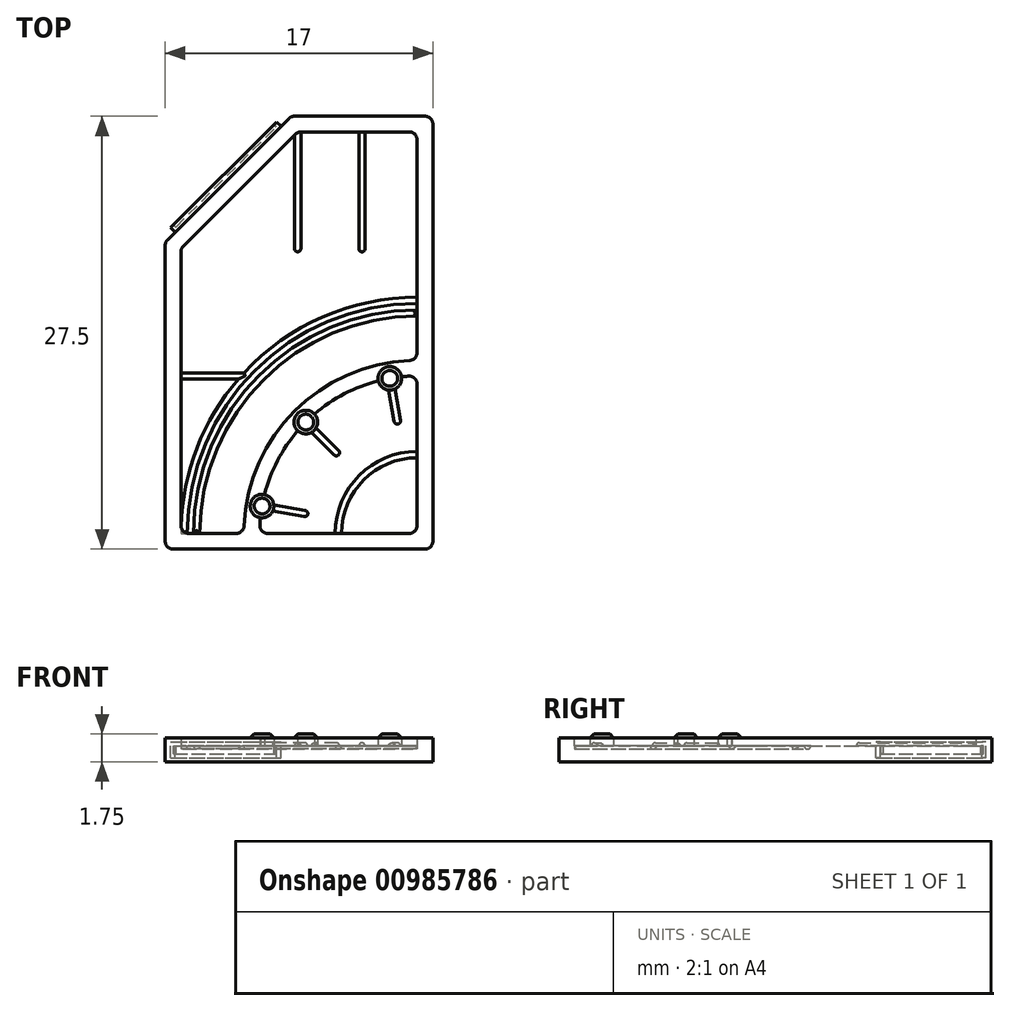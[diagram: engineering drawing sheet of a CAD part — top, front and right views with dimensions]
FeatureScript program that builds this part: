
annotation { "Feature Type Name" : "Feature", "Feature Type Description" : "" }
export const myFeature = defineFeature(function(context is Context, id is Id, definition is map)
    precondition{}
    {
        {
            var Q0;
            Q0=qCreatedBy(makeId("Top.planeOp"),FACE);
            var sketch = newSketch(context, id + "F0", { "sketchPlane" : qUnion([Q0])});
            skLineSegment(sketch, "E0.bottom", {"start": v(-8.5, -13.75) * mm, "end": v(8.5, -13.75) * mm});
            skLineSegment(sketch, "E0.top", {"start": v(-0.5, 13.75) * mm, "end": v(8.5, 13.75) * mm});
            skLineSegment(sketch, "E0.left", {"start": v(-8.5, -13.75) * mm, "end": v(-8.5, 5.75) * mm});
            skLineSegment(sketch, "E0.right", {"start": v(8.5, -13.75) * mm, "end": v(8.5, 13.75) * mm});
            skPoint(sketch, "E0.middle", {"position": v(0, 0) * mm});
            skLineSegment(sketch, "E1", {"start": v(-0.5, 13.75) * mm, "end": v(-8.5, 5.75) * mm});
            skPoint(sketch, "E2.orphan", {"position": v(-8.5, 13.75) * mm});
            skLineSegment(sketch, "E3", {"start": v(-0.5, 13.75) * mm, "end": v(-8.5, 13.75) * mm, "construction": true});
            skLineSegment(sketch, "E4.0", {"start": v(-7.5, -12.75) * mm, "end": v(-7.5, 5.34) * mm});
            skLineSegment(sketch, "E4.1", {"start": v(-0.09, 12.75) * mm, "end": v(-7.5, 5.34) * mm});
            skLineSegment(sketch, "E4.2", {"start": v(-7.5, -12.75) * mm, "end": v(-3.5, -12.75) * mm});
            skLineSegment(sketch, "E4.3", {"start": v(7.5, -12.75) * mm, "end": v(7.5, -2.75) * mm});
            skLineSegment(sketch, "E4.4", {"start": v(-0.09, 12.75) * mm, "end": v(7.5, 12.75) * mm});
            skArc(sketch, "E5", {"start": v(7.5, -2.75) * mm, "mid": v(7, -2.76) * mm, "end": v(6.5, -2.8) * mm});
            skArc(sketch, "E6.0", {"start": v(7.5, -1.75) * mm, "mid": v(-0.28, -4.97) * mm, "end": v(-3.5, -12.75) * mm});
            skLineSegment(sketch, "E7.trimOffspring", {"start": v(-2.5, -12.75) * mm, "end": v(7.5, -12.75) * mm});
            skLineSegment(sketch, "E8.trimOffspring", {"start": v(7.5, -1.75) * mm, "end": v(7.5, 12.75) * mm});
            skLineSegment(sketch, "E9", {"start": v(7.5, -12.75) * mm, "end": v(-2.35, -11.01) * mm, "construction": true});
            skLineSegment(sketch, "E10", {"start": v(7.5, -12.75) * mm, "end": v(0.43, -5.68) * mm, "construction": true});
            skLineSegment(sketch, "E11", {"start": v(7.5, -12.75) * mm, "end": v(5.76, -2.9) * mm, "construction": true});
            skCircle(sketch, "E12", {"center": v(5.76, -2.9) * mm, "radius": 0.75 * mm});
            skCircle(sketch, "E13", {"center": v(0.43, -5.68) * mm, "radius": 0.75 * mm});
            skCircle(sketch, "E14", {"center": v(-2.35, -11.01) * mm, "radius": 0.75 * mm});
            skArc(sketch, "E15.trimOffspring", {"start": v(-2.45, -11.76) * mm, "mid": v(-2.49, -12.25) * mm, "end": v(-2.5, -12.75) * mm});
            skArc(sketch, "E16.trimOffspring", {"start": v(-0.08, -6.23) * mm, "mid": v(-1.37, -8.13) * mm, "end": v(-2.2, -10.28) * mm});
            skArc(sketch, "E17.trimOffspring", {"start": v(5.03, -3.06) * mm, "mid": v(2.88, -3.88) * mm, "end": v(0.98, -5.17) * mm});
            skLineSegment(sketch, "E18", {"start": v(4, 12.75) * mm, "end": v(4, 5.34) * mm, "construction": true});
            skPoint(sketch, "E18.startSnap0", {"position": v(4, 13.75) * mm});
            skLineSegment(sketch, "E19", {"start": v(-0.09, 12.75) * mm, "end": v(-0.09, 5.34) * mm, "construction": true});
            skArc(sketch, "E20.0", {"start": v(7.5, 1.25) * mm, "mid": v(-2.4, -2.85) * mm, "end": v(-6.5, -12.75) * mm, "construction": true});
            skArc(sketch, "E21.0", {"start": v(7.5, 2.05) * mm, "mid": v(-2.97, -2.28) * mm, "end": v(-7.3, -12.75) * mm, "construction": true});
            skLineSegment(sketch, "E22", {"start": v(-7.5, -2.75) * mm, "end": v(-3.41, -2.75) * mm, "construction": true});
            skLineSegment(sketch, "E23", {"start": v(-7.5, -2.75) * mm, "end": v(-7.5, -12.75) * mm, "construction": true});
            skLineSegment(sketch, "E24", {"start": v(5.9, -3.64) * mm, "end": v(6.24, -5.61) * mm});
            skLineSegment(sketch, "E25", {"start": v(0.96, -6.2) * mm, "end": v(2.37, -7.62) * mm});
            skLineSegment(sketch, "E26", {"start": v(-1.6, -11.14) * mm, "end": v(0.36, -11.5) * mm});
            skArc(sketch, "E27", {"start": v(7.5, -7.75) * mm, "mid": v(3.96, -9.21) * mm, "end": v(2.5, -12.75) * mm, "construction": true});
            skLineSegment(sketch, "E28.0", {"start": v(-0.29, 12.75) * mm, "end": v(-0.29, 5.34) * mm});
            skLineSegment(sketch, "E29.0", {"start": v(0.11, 12.75) * mm, "end": v(0.11, 5.34) * mm});
            skLineSegment(sketch, "E30.0", {"start": v(3.8, 12.75) * mm, "end": v(3.8, 5.34) * mm});
            skLineSegment(sketch, "E31.0", {"start": v(4.2, 12.75) * mm, "end": v(4.2, 5.34) * mm});
            skArc(sketch, "E32", {"start": v(0.11, 5.34) * mm, "mid": v(-0.09, 5.14) * mm, "end": v(-0.29, 5.34) * mm});
            skArc(sketch, "E33", {"start": v(4.2, 5.34) * mm, "mid": v(4, 5.14) * mm, "end": v(3.8, 5.34) * mm});
            skArc(sketch, "E34.0", {"start": v(7.5, 1.45) * mm, "mid": v(-2.54, -2.7) * mm, "end": v(-6.7, -12.75) * mm});
            skArc(sketch, "E35.0", {"start": v(7.5, 1.05) * mm, "mid": v(-2.26, -3) * mm, "end": v(-6.3, -12.75) * mm});
            skArc(sketch, "E36.0", {"start": v(7.5, 2.25) * mm, "mid": v(1.5, 1) * mm, "end": v(-3.5, -2.55) * mm});
            skArc(sketch, "E37.0", {"start": v(7.5, 1.85) * mm, "mid": v(-2.82, -2.43) * mm, "end": v(-7.1, -12.75) * mm});
            skLineSegment(sketch, "E38.0", {"start": v(-7.5, -2.95) * mm, "end": v(-3.86, -2.95) * mm});
            skLineSegment(sketch, "E39.0", {"start": v(-7.5, -2.55) * mm, "end": v(-3.5, -2.55) * mm});
            skArc(sketch, "E40.trimOffspring", {"start": v(-3.86, -2.95) * mm, "mid": v(-6.56, -7.52) * mm, "end": v(-7.5, -12.75) * mm});
            skLineSegment(sketch, "E41.0", {"start": v(5.7, -3.65) * mm, "end": v(6.04, -5.64) * mm});
            skLineSegment(sketch, "E42.0", {"start": v(6.09, -3.58) * mm, "end": v(6.44, -5.58) * mm});
            skLineSegment(sketch, "E43.0", {"start": v(0.8, -6.33) * mm, "end": v(2.23, -7.76) * mm});
            skLineSegment(sketch, "E44.0", {"start": v(1.08, -6.05) * mm, "end": v(2.51, -7.48) * mm});
            skLineSegment(sketch, "E45.0", {"start": v(-1.67, -11.34) * mm, "end": v(0.33, -11.69) * mm});
            skLineSegment(sketch, "E46.0", {"start": v(-1.6, -10.94) * mm, "end": v(0.4, -11.3) * mm});
            skArc(sketch, "E47", {"start": v(0.4, -11.3) * mm, "mid": v(0.56, -11.53) * mm, "end": v(0.33, -11.69) * mm});
            skArc(sketch, "E48", {"start": v(2.51, -7.48) * mm, "mid": v(2.51, -7.76) * mm, "end": v(2.23, -7.76) * mm});
            skArc(sketch, "E49", {"start": v(6.44, -5.58) * mm, "mid": v(6.28, -5.8) * mm, "end": v(6.04, -5.64) * mm});
            skArc(sketch, "E50.0", {"start": v(7.5, -7.55) * mm, "mid": v(3.82, -9.07) * mm, "end": v(2.3, -12.75) * mm});
            skArc(sketch, "E51.0", {"start": v(7.5, -7.95) * mm, "mid": v(4.1, -9.36) * mm, "end": v(2.7, -12.75) * mm});
            skSolve(sketch);
        }
        {
            var Q0;
            Q0=makeQuery(id+"F0.imprint","IMPRINT",FACE,{"disambiguationData":[TD([[makeQuery(id+"F0.imprint","IMPRINT",EDGE,{"derivedFrom":sQuery(id+"F0.wireOp",EDGE,"E4.0")}),-1.0]])]});
            var Q1;
            Q1=makeQuery(id+"F0.imprint","IMPRINT",FACE,{"disambiguationData":[TD([[makeQuery(id+"F0.imprint","IMPRINT",EDGE,{"derivedFrom":sQuery(id+"F0.wireOp",EDGE,"E4.3")}),1.0]])]});
            var Q2;
            Q2=makeQuery(id+"F0.imprint","IMPRINT",FACE,{"disambiguationData":[TD([[makeQuery(id+"F0.imprint","IMPRINT",EDGE,{"derivedFrom":sQuery(id+"F0.wireOp",EDGE,"E0.bottom")}),1.0]])]});
            var Q3;
            {var subQ0=sQuery(id+"F0.wireOp",EDGE,"E13");var subQ1=makeQuery(id+"F0.imprint","INTERSECT",VERTEX,{"derivedFrom":[subQ0,sQuery(id+"F0.wireOp",EDGE,"E16.trimOffspring")]});Q3=makeQuery(id+"F0.imprint","IMPRINT",FACE,{"disambiguationData":[TD([[makeQuery(id+"F0.imprint","IMPRINT",EDGE,{"disambiguationData":[TD([[subQ1,1.0]])],"derivedFrom":subQ0}),1.0]])]});}
            var Q4;
            {var subQ0=sQuery(id+"F0.wireOp",EDGE,"E12");var subQ1=makeQuery(id+"F0.imprint","INTERSECT",VERTEX,{"derivedFrom":[sQuery(id+"F0.wireOp",EDGE,"E5"),subQ0]});Q4=makeQuery(id+"F0.imprint","IMPRINT",FACE,{"disambiguationData":[TD([[makeQuery(id+"F0.imprint","IMPRINT",EDGE,{"disambiguationData":[TD([[subQ1,-1.0]])],"derivedFrom":subQ0}),1.0]])]});}
            var Q5;
            {var subQ0=sQuery(id+"F0.wireOp",EDGE,"E14");var subQ1=makeQuery(id+"F0.imprint","INTERSECT",VERTEX,{"derivedFrom":[subQ0,sQuery(id+"F0.wireOp",EDGE,"E15.trimOffspring")]});Q5=makeQuery(id+"F0.imprint","IMPRINT",FACE,{"disambiguationData":[TD([[makeQuery(id+"F0.imprint","IMPRINT",EDGE,{"disambiguationData":[TD([[subQ1,1.0]])],"derivedFrom":subQ0}),1.0]])]});}
            var Q6;
            {var subQ5=sQuery(id+"F0.wireOp",EDGE,"E22");Q6=makeQuery(id+"F0.imprint","IMPRINT",FACE,{"disambiguationData":[TD([[makeQuery(id+"F0.imprint","IMPRINT",EDGE,{"derivedFrom":subQ5}),1.0]])]});}
            var Q7;
            {var subQ6=sQuery(id+"F0.wireOp",EDGE,"E29.0");Q7=makeQuery(id+"F0.imprint","IMPRINT",FACE,{"disambiguationData":[TD([[makeQuery(id+"F0.imprint","IMPRINT",EDGE,{"derivedFrom":subQ6}),-1.0]])]});}
            var Q8;
            {var subQ0=sQuery(id+"F0.wireOp",EDGE,"E30.0");Q8=makeQuery(id+"F0.imprint","IMPRINT",FACE,{"disambiguationData":[TD([[makeQuery(id+"F0.imprint","IMPRINT",EDGE,{"derivedFrom":subQ0}),1.0]])]});}
            var Q9;
            {var subQ0=sQuery(id+"F0.wireOp",EDGE,"E20.0");Q9=makeQuery(id+"F0.imprint","IMPRINT",FACE,{"disambiguationData":[TD([[makeQuery(id+"F0.imprint","IMPRINT",EDGE,{"derivedFrom":subQ0}),-1.0]])]});}
            var Q10;
            {var subQ0=sQuery(id+"F0.wireOp",EDGE,"E6.0");Q10=makeQuery(id+"F0.imprint","IMPRINT",FACE,{"disambiguationData":[TD([[makeQuery(id+"F0.imprint","IMPRINT",EDGE,{"derivedFrom":subQ0}),-1.0]])]});}
            var Q11;
            {var subQ8=sQuery(id+"F0.wireOp",EDGE,"E5");Q11=makeQuery(id+"F0.imprint","IMPRINT",FACE,{"disambiguationData":[TD([[makeQuery(id+"F0.imprint","IMPRINT",EDGE,{"derivedFrom":subQ8}),1.0]])]});}
            var Q12;
            {var subQ0=sQuery(id+"F0.wireOp",EDGE,"E34.0");Q12=makeQuery(id+"F0.imprint","IMPRINT",FACE,{"disambiguationData":[TD([[makeQuery(id+"F0.imprint","IMPRINT",EDGE,{"derivedFrom":subQ0}),1.0]])]});}
            var Q13;
            {var subQ0=sQuery(id+"F0.wireOp",EDGE,"E34.0");Q13=makeQuery(id+"F0.imprint","IMPRINT",FACE,{"disambiguationData":[TD([[makeQuery(id+"F0.imprint","IMPRINT",EDGE,{"derivedFrom":subQ0}),-1.0]])]});}
            var Q14;
            {var subQ0=sQuery(id+"F0.wireOp",EDGE,"E36.0");Q14=makeQuery(id+"F0.imprint","IMPRINT",FACE,{"disambiguationData":[TD([[makeQuery(id+"F0.imprint","IMPRINT",EDGE,{"derivedFrom":subQ0}),1.0]])]});}
            var Q15;
            {var subQ0=sQuery(id+"F0.wireOp",EDGE,"E29.0");Q15=makeQuery(id+"F0.imprint","IMPRINT",FACE,{"disambiguationData":[TD([[makeQuery(id+"F0.imprint","IMPRINT",EDGE,{"derivedFrom":subQ0}),1.0]])]});}
            var Q16;
            {var subQ1=sQuery(id+"F0.wireOp",EDGE,"E43.0");Q16=makeQuery(id+"F0.imprint","IMPRINT",FACE,{"disambiguationData":[TD([[makeQuery(id+"F0.imprint","IMPRINT",EDGE,{"derivedFrom":subQ1}),1.0]])]});}
            var Q17;
            {var subQ0=sQuery(id+"F0.wireOp",EDGE,"E41.0");Q17=makeQuery(id+"F0.imprint","IMPRINT",FACE,{"disambiguationData":[TD([[makeQuery(id+"F0.imprint","IMPRINT",EDGE,{"derivedFrom":subQ0}),1.0]])]});}
            var Q18;
            {var subQ0=sQuery(id+"F0.wireOp",EDGE,"E50.0");Q18=makeQuery(id+"F0.imprint","IMPRINT",FACE,{"disambiguationData":[TD([[makeQuery(id+"F0.imprint","IMPRINT",EDGE,{"derivedFrom":subQ0}),1.0]])]});}
            var Q19;
            {var subQ3=sQuery(id+"F0.wireOp",EDGE,"E45.0");Q19=makeQuery(id+"F0.imprint","IMPRINT",FACE,{"disambiguationData":[TD([[makeQuery(id+"F0.imprint","IMPRINT",EDGE,{"derivedFrom":subQ3}),1.0]])]});}
            extrude(context, id + "F1", {"entities" : qUnion([Q0, Q1, Q2, Q3, Q4, Q5, Q6, Q7, Q8, Q9, Q10, Q11, Q12, Q13, Q14, Q15, Q16, Q17, Q18, Q19]), "oppositeDirection" : true, "depth" : 1 * mm, "offsetDistance" : 25 * mm});
        }
        {
            var Q0;
            Q0=makeQuery(id+"F0.imprint","IMPRINT",FACE,{"disambiguationData":[TD([[makeQuery(id+"F0.imprint","IMPRINT",EDGE,{"derivedFrom":sQuery(id+"F0.wireOp",EDGE,"E0.bottom")}),1.0]])]});
            extrude(context, id + "F2", {"entities" : qUnion([Q0]), "operationType" : NewBodyOperationType.ADD, "depth" : .5 * mm, "offsetDistance" : 25 * mm});
        }
        {
            var Q0;
            {var subQ0=sQuery(id+"F0.wireOp",EDGE,"E14");var subQ1=makeQuery(id+"F0.imprint","INTERSECT",VERTEX,{"derivedFrom":[subQ0,sQuery(id+"F0.wireOp",EDGE,"E15.trimOffspring")]});Q0=makeQuery(id+"F0.imprint","IMPRINT",FACE,{"disambiguationData":[TD([[makeQuery(id+"F0.imprint","IMPRINT",EDGE,{"disambiguationData":[TD([[subQ1,1.0]])],"derivedFrom":subQ0}),1.0]])]});}
            var Q1;
            {var subQ0=sQuery(id+"F0.wireOp",EDGE,"E13");var subQ1=makeQuery(id+"F0.imprint","INTERSECT",VERTEX,{"derivedFrom":[subQ0,sQuery(id+"F0.wireOp",EDGE,"E16.trimOffspring")]});Q1=makeQuery(id+"F0.imprint","IMPRINT",FACE,{"disambiguationData":[TD([[makeQuery(id+"F0.imprint","IMPRINT",EDGE,{"disambiguationData":[TD([[subQ1,1.0]])],"derivedFrom":subQ0}),1.0]])]});}
            var Q2;
            {var subQ0=sQuery(id+"F0.wireOp",EDGE,"E12");var subQ1=makeQuery(id+"F0.imprint","INTERSECT",VERTEX,{"derivedFrom":[sQuery(id+"F0.wireOp",EDGE,"E5"),subQ0]});Q2=makeQuery(id+"F0.imprint","IMPRINT",FACE,{"disambiguationData":[TD([[makeQuery(id+"F0.imprint","IMPRINT",EDGE,{"disambiguationData":[TD([[subQ1,-1.0]])],"derivedFrom":subQ0}),1.0]])]});}
            extrude(context, id + "F3", {"entities" : qUnion([Q0, Q1, Q2]), "operationType" : NewBodyOperationType.ADD, "depth" : .75 * mm, "offsetDistance" : 25 * mm});
        }
        {
            var Q0;
            Q0=makeQuery(id+"F3.opExtrude","CAP_EDGE",EDGE,{"disambiguationData":[OSD([sQuery(id+"F0.wireOp",EDGE,"E12")])],"isStart":false});
            var Q1;
            Q1=makeQuery(id+"F3.opExtrude","CAP_FACE",FACE,{"disambiguationData":[OSD([sQuery(id+"F0.wireOp",EDGE,"E13")])],"isStart":false});
            var Q2;
            Q2=makeQuery(id+"F3.opExtrude","CAP_FACE",FACE,{"disambiguationData":[OSD([sQuery(id+"F0.wireOp",EDGE,"E14")])],"isStart":false});
            chamfer(context, id + "F4", {"entities" : qUnion([Q0, Q1, Q2]), "width" : .25 * mm, "tangentPropagation" : true});
        }
        {
            var Q0;
            {var subQ0=sQuery(id+"F0.wireOp",EDGE,"E1");var subQ1=sQuery(id+"F0.wireOp",EDGE,"E0.left");Q0=makeQuery(id+"F2.boolean.opBoolean","MERGE",EDGE,{"derivedFrom":[makeQuery(id+"F1.opExtrude","SWEPT_EDGE",EDGE,{"disambiguationData":[OSD([subQ1,subQ0])]}),makeQuery(id+"F2.opExtrude","SWEPT_EDGE",EDGE,{"disambiguationData":[OSD([subQ1,subQ0])]})]});}
            var Q1;
            {var subQ0=sQuery(id+"F0.wireOp",EDGE,"E0.left");var subQ1=sQuery(id+"F0.wireOp",EDGE,"E0.bottom");Q1=makeQuery(id+"F2.boolean.opBoolean","MERGE",EDGE,{"derivedFrom":[makeQuery(id+"F1.opExtrude","SWEPT_EDGE",EDGE,{"disambiguationData":[OSD([subQ1,subQ0])]}),makeQuery(id+"F2.opExtrude","SWEPT_EDGE",EDGE,{"disambiguationData":[OSD([subQ1,subQ0])]})]});}
            var Q2;
            {var subQ0=sQuery(id+"F0.wireOp",EDGE,"E0.right");var subQ1=sQuery(id+"F0.wireOp",EDGE,"E0.bottom");Q2=makeQuery(id+"F2.boolean.opBoolean","MERGE",EDGE,{"derivedFrom":[makeQuery(id+"F1.opExtrude","SWEPT_EDGE",EDGE,{"disambiguationData":[OSD([subQ1,subQ0])]}),makeQuery(id+"F2.opExtrude","SWEPT_EDGE",EDGE,{"disambiguationData":[OSD([subQ1,subQ0])]})]});}
            var Q3;
            {var subQ0=sQuery(id+"F0.wireOp",EDGE,"E0.right");var subQ1=sQuery(id+"F0.wireOp",EDGE,"E0.top");Q3=makeQuery(id+"F2.boolean.opBoolean","MERGE",EDGE,{"derivedFrom":[makeQuery(id+"F1.opExtrude","SWEPT_EDGE",EDGE,{"disambiguationData":[OSD([subQ1,subQ0])]}),makeQuery(id+"F2.opExtrude","SWEPT_EDGE",EDGE,{"disambiguationData":[OSD([subQ1,subQ0])]})]});}
            var Q4;
            {var subQ0=sQuery(id+"F0.wireOp",EDGE,"E1");var subQ1=sQuery(id+"F0.wireOp",EDGE,"E0.top");Q4=makeQuery(id+"F2.boolean.opBoolean","MERGE",EDGE,{"derivedFrom":[makeQuery(id+"F1.opExtrude","SWEPT_EDGE",EDGE,{"disambiguationData":[OSD([subQ1,subQ0])]}),makeQuery(id+"F2.opExtrude","SWEPT_EDGE",EDGE,{"disambiguationData":[OSD([subQ1,subQ0])]})]});}
            var Q5;
            Q5=makeQuery(id+"F2.opExtrude","SWEPT_EDGE",EDGE,{"disambiguationData":[OSD([sQuery(id+"F0.wireOp",EDGE,"E4.4"),sQuery(id+"F0.wireOp",EDGE,"E8.trimOffspring")])]});
            var Q6;
            Q6=makeQuery(id+"F2.opExtrude","SWEPT_EDGE",EDGE,{"disambiguationData":[OSD([sQuery(id+"F0.wireOp",EDGE,"E4.1"),sQuery(id+"F0.wireOp",EDGE,"E4.4")])]});
            var Q7;
            Q7=makeQuery(id+"F2.opExtrude","SWEPT_EDGE",EDGE,{"disambiguationData":[OSD([sQuery(id+"F0.wireOp",EDGE,"E4.0"),sQuery(id+"F0.wireOp",EDGE,"E4.1")])]});
            var Q8;
            Q8=makeQuery(id+"F2.opExtrude","SWEPT_EDGE",EDGE,{"disambiguationData":[OSD([sQuery(id+"F0.wireOp",EDGE,"E4.0"),sQuery(id+"F0.wireOp",EDGE,"E4.2")])]});
            var Q9;
            Q9=makeQuery(id+"F2.opExtrude","SWEPT_EDGE",EDGE,{"disambiguationData":[OSD([sQuery(id+"F0.wireOp",EDGE,"E4.2"),sQuery(id+"F0.wireOp",EDGE,"E6.0")])]});
            var Q10;
            Q10=makeQuery(id+"F2.opExtrude","SWEPT_EDGE",EDGE,{"disambiguationData":[OSD([sQuery(id+"F0.wireOp",EDGE,"E6.0"),sQuery(id+"F0.wireOp",EDGE,"E8.trimOffspring")])]});
            var Q11;
            Q11=makeQuery(id+"F2.opExtrude","SWEPT_EDGE",EDGE,{"disambiguationData":[OSD([sQuery(id+"F0.wireOp",EDGE,"E7.trimOffspring"),sQuery(id+"F0.wireOp",EDGE,"E15.trimOffspring")])]});
            var Q12;
            Q12=makeQuery(id+"F2.opExtrude","SWEPT_EDGE",EDGE,{"disambiguationData":[OSD([sQuery(id+"F0.wireOp",EDGE,"E4.3"),sQuery(id+"F0.wireOp",EDGE,"E5")])]});
            var Q13;
            Q13=makeQuery(id+"F2.opExtrude","SWEPT_EDGE",EDGE,{"disambiguationData":[OSD([sQuery(id+"F0.wireOp",EDGE,"E4.3"),sQuery(id+"F0.wireOp",EDGE,"E7.trimOffspring")])]});
            fillet(context, id + "F5", {"entities" : qUnion([Q0, Q1, Q2, Q3, Q4, Q5, Q6, Q7, Q8, Q9, Q10, Q11, Q12, Q13]), "radius" : .5 * mm, "tangentPropagation" : true, "allowEdgeOverflow" : false});
        }
        {
            var Q0;
            {var subQ6=sQuery(id+"F0.wireOp",EDGE,"E29.0");Q0=makeQuery(id+"F0.imprint","IMPRINT",FACE,{"disambiguationData":[TD([[makeQuery(id+"F0.imprint","IMPRINT",EDGE,{"derivedFrom":subQ6}),-1.0]])]});}
            var Q1;
            {var subQ0=sQuery(id+"F0.wireOp",EDGE,"E30.0");Q1=makeQuery(id+"F0.imprint","IMPRINT",FACE,{"disambiguationData":[TD([[makeQuery(id+"F0.imprint","IMPRINT",EDGE,{"derivedFrom":subQ0}),1.0]])]});}
            var Q2;
            {var subQ3=sQuery(id+"F0.wireOp",EDGE,"E45.0");Q2=makeQuery(id+"F0.imprint","IMPRINT",FACE,{"disambiguationData":[TD([[makeQuery(id+"F0.imprint","IMPRINT",EDGE,{"derivedFrom":subQ3}),1.0]])]});}
            var Q3;
            {var subQ1=sQuery(id+"F0.wireOp",EDGE,"E43.0");Q3=makeQuery(id+"F0.imprint","IMPRINT",FACE,{"disambiguationData":[TD([[makeQuery(id+"F0.imprint","IMPRINT",EDGE,{"derivedFrom":subQ1}),1.0]])]});}
            var Q4;
            {var subQ0=sQuery(id+"F0.wireOp",EDGE,"E41.0");Q4=makeQuery(id+"F0.imprint","IMPRINT",FACE,{"disambiguationData":[TD([[makeQuery(id+"F0.imprint","IMPRINT",EDGE,{"derivedFrom":subQ0}),1.0]])]});}
            extrude(context, id + "F6", {"entities" : qUnion([Q0, Q1, Q2, Q3, Q4]), "operationType" : NewBodyOperationType.ADD, "depth" : .2 * mm, "offsetDistance" : 25 * mm});
        }
        {
            var Q0;
            Q0=makeQuery(id+"F6.opExtrude","CAP_EDGE",EDGE,{"disambiguationData":[OSD([sQuery(id+"F0.wireOp",EDGE,"E28.0")])],"isStart":false});
            var Q1;
            Q1=makeQuery(id+"F6.opExtrude","CAP_EDGE",EDGE,{"disambiguationData":[OSD([sQuery(id+"F0.wireOp",EDGE,"E30.0")])],"isStart":false});
            var Q2;
            Q2=makeQuery(id+"F6.opExtrude","CAP_EDGE",EDGE,{"disambiguationData":[OSD([sQuery(id+"F0.wireOp",EDGE,"E45.0")])],"isStart":false});
            var Q3;
            Q3=makeQuery(id+"F6.opExtrude","CAP_EDGE",EDGE,{"disambiguationData":[OSD([sQuery(id+"F0.wireOp",EDGE,"E43.0")])],"isStart":false});
            var Q4;
            Q4=makeQuery(id+"F6.opExtrude","CAP_EDGE",EDGE,{"disambiguationData":[OSD([sQuery(id+"F0.wireOp",EDGE,"E41.0")])],"isStart":false});
            fillet(context, id + "F7", {"entities" : qUnion([Q0, Q1, Q2, Q3, Q4]), "radius" : .2 * mm, "tangentPropagation" : true, "allowEdgeOverflow" : false});
        }
        {
            var Q0;
            {var subQ0=sQuery(id+"F0.wireOp",EDGE,"E34.0");Q0=makeQuery(id+"F0.imprint","IMPRINT",FACE,{"disambiguationData":[TD([[makeQuery(id+"F0.imprint","IMPRINT",EDGE,{"derivedFrom":subQ0}),1.0]])]});}
            var Q1;
            {var subQ0=sQuery(id+"F0.wireOp",EDGE,"E36.0");Q1=makeQuery(id+"F0.imprint","IMPRINT",FACE,{"disambiguationData":[TD([[makeQuery(id+"F0.imprint","IMPRINT",EDGE,{"derivedFrom":subQ0}),1.0]])]});}
            var Q2;
            {var subQ0=sQuery(id+"F0.wireOp",EDGE,"E50.0");Q2=makeQuery(id+"F0.imprint","IMPRINT",FACE,{"disambiguationData":[TD([[makeQuery(id+"F0.imprint","IMPRINT",EDGE,{"derivedFrom":subQ0}),1.0]])]});}
            extrude(context, id + "F8", {"entities" : qUnion([Q0, Q1, Q2]), "operationType" : NewBodyOperationType.REMOVE, "oppositeDirection" : true, "depth" : .2 * mm, "offsetDistance" : 25 * mm});
        }
        {
            var Q0;
            Q0=makeQuery(id+"F8.boolean.opBoolean","COPY",EDGE,{"derivedFrom":makeQuery(id+"F8.opExtrude","CAP_EDGE",EDGE,{"disambiguationData":[OSD([sQuery(id+"F0.wireOp",EDGE,"E36.0")])],"isStart":false})});
            var Q1;
            Q1=makeQuery(id+"F8.boolean.opBoolean","COPY",EDGE,{"derivedFrom":makeQuery(id+"F8.opExtrude","CAP_EDGE",EDGE,{"disambiguationData":[OSD([sQuery(id+"F0.wireOp",EDGE,"E39.0")])],"isStart":false})});
            var Q2;
            Q2=makeQuery(id+"F8.boolean.opBoolean","COPY",EDGE,{"derivedFrom":makeQuery(id+"F8.opExtrude","CAP_EDGE",EDGE,{"disambiguationData":[OSD([sQuery(id+"F0.wireOp",EDGE,"E38.0")])],"isStart":false})});
            var Q3;
            Q3=makeQuery(id+"F8.boolean.opBoolean","COPY",EDGE,{"derivedFrom":makeQuery(id+"F8.opExtrude","CAP_EDGE",EDGE,{"disambiguationData":[OSD([sQuery(id+"F0.wireOp",EDGE,"E37.0")])],"isStart":false})});
            var Q4;
            Q4=makeQuery(id+"F8.boolean.opBoolean","COPY",EDGE,{"derivedFrom":makeQuery(id+"F8.opExtrude","CAP_EDGE",EDGE,{"disambiguationData":[OSD([sQuery(id+"F0.wireOp",EDGE,"E40.trimOffspring")])],"isStart":false})});
            var Q5;
            Q5=makeQuery(id+"F8.boolean.opBoolean","COPY",EDGE,{"derivedFrom":makeQuery(id+"F8.opExtrude","CAP_EDGE",EDGE,{"disambiguationData":[OSD([sQuery(id+"F0.wireOp",EDGE,"E34.0")])],"isStart":false})});
            var Q6;
            Q6=makeQuery(id+"F8.boolean.opBoolean","COPY",FACE,{"derivedFrom":makeQuery(id+"F8.opExtrude","CAP_FACE",FACE,{"disambiguationData":[OSD([sQuery(id+"F0.wireOp",EDGE,"E4.2"),sQuery(id+"F0.wireOp",EDGE,"E8.trimOffspring"),sQuery(id+"F0.wireOp",EDGE,"E34.0"),sQuery(id+"F0.wireOp",EDGE,"E35.0")])],"isStart":false})});
            var Q7;
            Q7=makeQuery(id+"F8.boolean.opBoolean","COPY",EDGE,{"derivedFrom":makeQuery(id+"F8.opExtrude","CAP_EDGE",EDGE,{"disambiguationData":[OSD([sQuery(id+"F0.wireOp",EDGE,"E50.0")])],"isStart":false})});
            var Q8;
            Q8=makeQuery(id+"F8.boolean.opBoolean","COPY",EDGE,{"derivedFrom":makeQuery(id+"F8.opExtrude","CAP_EDGE",EDGE,{"disambiguationData":[OSD([sQuery(id+"F0.wireOp",EDGE,"E51.0")])],"isStart":false})});
            fillet(context, id + "F9", {"entities" : qUnion([Q0, Q1, Q2, Q3, Q4, Q5, Q6, Q7, Q8]), "radius" : .2 * mm, "tangentPropagation" : true, "allowEdgeOverflow" : false});
        }
        {
            var Q0;
            {var subQ0=sQuery(id+"F0.wireOp",EDGE,"E1");Q0=makeQuery(id+"F2.boolean.opBoolean","MERGE",FACE,{"derivedFrom":[makeQuery(id+"F1.opExtrude","SWEPT_FACE",FACE,{"disambiguationData":[OSD([subQ0])]}),makeQuery(id+"F2.opExtrude","SWEPT_FACE",FACE,{"disambiguationData":[OSD([subQ0])]})]});}
            var sketch = newSketch(context, id + "F10", { "sketchPlane" : qUnion([Q0])});
            skLineSegment(sketch, "E52.bottom", {"start": v(1.04, -0.75) * mm, "end": v(-8.46, -0.75) * mm});
            skLineSegment(sketch, "E52.top", {"start": v(1.04, 0.25) * mm, "end": v(-8.46, 0.25) * mm});
            skLineSegment(sketch, "E52.left", {"start": v(1.04, -0.75) * mm, "end": v(1.04, 0.25) * mm});
            skLineSegment(sketch, "E52.right", {"start": v(-8.46, -0.75) * mm, "end": v(-8.46, 0.25) * mm});
            skPoint(sketch, "E52.middle", {"position": v(-3.71, -0.25) * mm});
            skPoint(sketch, "E52.middle.positionSnap0", {"position": v(1.74, -0.25) * mm});
            skPoint(sketch, "E52.middle.positionSnap1", {"position": v(-3.71, 0.5) * mm});
            skPoint(sketch, "E52.centerSnap0", {"position": v(1.74, -0.25) * mm});
            skPoint(sketch, "E52.centerSnap1", {"position": v(-3.71, 0.5) * mm});
            skLineSegment(sketch, "E53.0", {"start": v(0.79, 0) * mm, "end": v(-8.21, 0) * mm});
            skLineSegment(sketch, "E53.1", {"start": v(0.79, -0.5) * mm, "end": v(0.79, 0) * mm});
            skLineSegment(sketch, "E53.2", {"start": v(0.79, -0.5) * mm, "end": v(-8.21, -0.5) * mm});
            skLineSegment(sketch, "E53.3", {"start": v(-8.21, -0.5) * mm, "end": v(-8.21, 0) * mm});
            skSolve(sketch);
        }
        {
            var Q0;
            Q0=makeQuery(id+"F10.imprint","IMPRINT",FACE,{"disambiguationData":[TD([[makeQuery(id+"F10.imprint","IMPRINT",EDGE,{"derivedFrom":sQuery(id+"F10.wireOp",EDGE,"E52.bottom")}),-1.0]])]});
            extrude(context, id + "F11", {"entities" : qUnion([Q0]), "operationType" : NewBodyOperationType.ADD, "depth" : .4 * mm, "offsetDistance" : 25 * mm});
        }
        {
            var Q0;
            {var subQ0=sQuery(id+"F0.wireOp",EDGE,"E1");Q0=makeQuery(id+"F11.boolean.opBoolean","SPLIT",FACE,{"disambiguationData":[TD([makeQuery(id+"F11.opExtrude","SWEPT_FACE",FACE,{"disambiguationData":[OSD([sQuery(id+"F10.wireOp",EDGE,"E53.0")])]})])],"derivedFrom":makeQuery(id+"F2.boolean.opBoolean","MERGE",FACE,{"derivedFrom":[makeQuery(id+"F1.opExtrude","SWEPT_FACE",FACE,{"disambiguationData":[OSD([subQ0])]}),makeQuery(id+"F2.opExtrude","SWEPT_FACE",FACE,{"disambiguationData":[OSD([subQ0])]})]})});}
            extrude(context, id + "F12", {"entities" : qUnion([Q0]), "operationType" : NewBodyOperationType.ADD, "depth" : .2 * mm, "offsetDistance" : 25 * mm});
        }
    });
